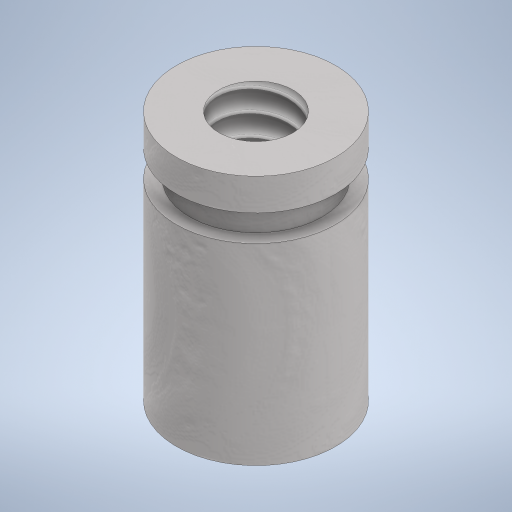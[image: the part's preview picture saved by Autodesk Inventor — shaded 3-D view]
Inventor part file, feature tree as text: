
AUTODESK INVENTOR PART (.ipt)
format: ipt  version: 2023 (Build 270158000, 158)  size: 306,176 bytes
history: native  units: mm
features: sketch x4, extrude x3, other x1, hole x1, thread x1
ambient origin geometry x8: Origin, YZ Plane, XZ Plane, XY Plane, X Axis, Y Axis, Z Axis, Center Point
bodies: Body1 (feature_tree)
feature tree (10):
  other  "Sólido1"
  extrude  "Extrusão1"  Depth=36.24mm TaperAngle=0.0deg
  extrude  "Extrusão2"  Depth=5.0mm TaperAngle=0.0deg
  extrude  "Extrusão3"  Depth=47.24mm
  hole  "Hole2"  [1 undecoded]
  thread  "Thread1"  [1 undecoded]
  sketch  "Esboço1"  dims[d0=30.0mm d1=36.24mm d2=0.0mm]
  sketch  "Esboço2"  dims[d3=25.0mm d4=5.0mm d5=0.0mm]
  sketch  "Esboço3"  dims[d6=6.0mm d7=0.0mm]
  sketch  "Sketch5"  dims[d15=14.0mm d16=6.0mm d17=4.0mm d18=2.0mm d19=90.0deg d20=0.5mm d21=20.594885mm d22=47.24mm d23=0.0mm]
note: 2 required parameter values undecoded (feature->parameter linkage not recoverable at this tier; creation-order binding heuristic only, values carry confidence <= 0.55)
